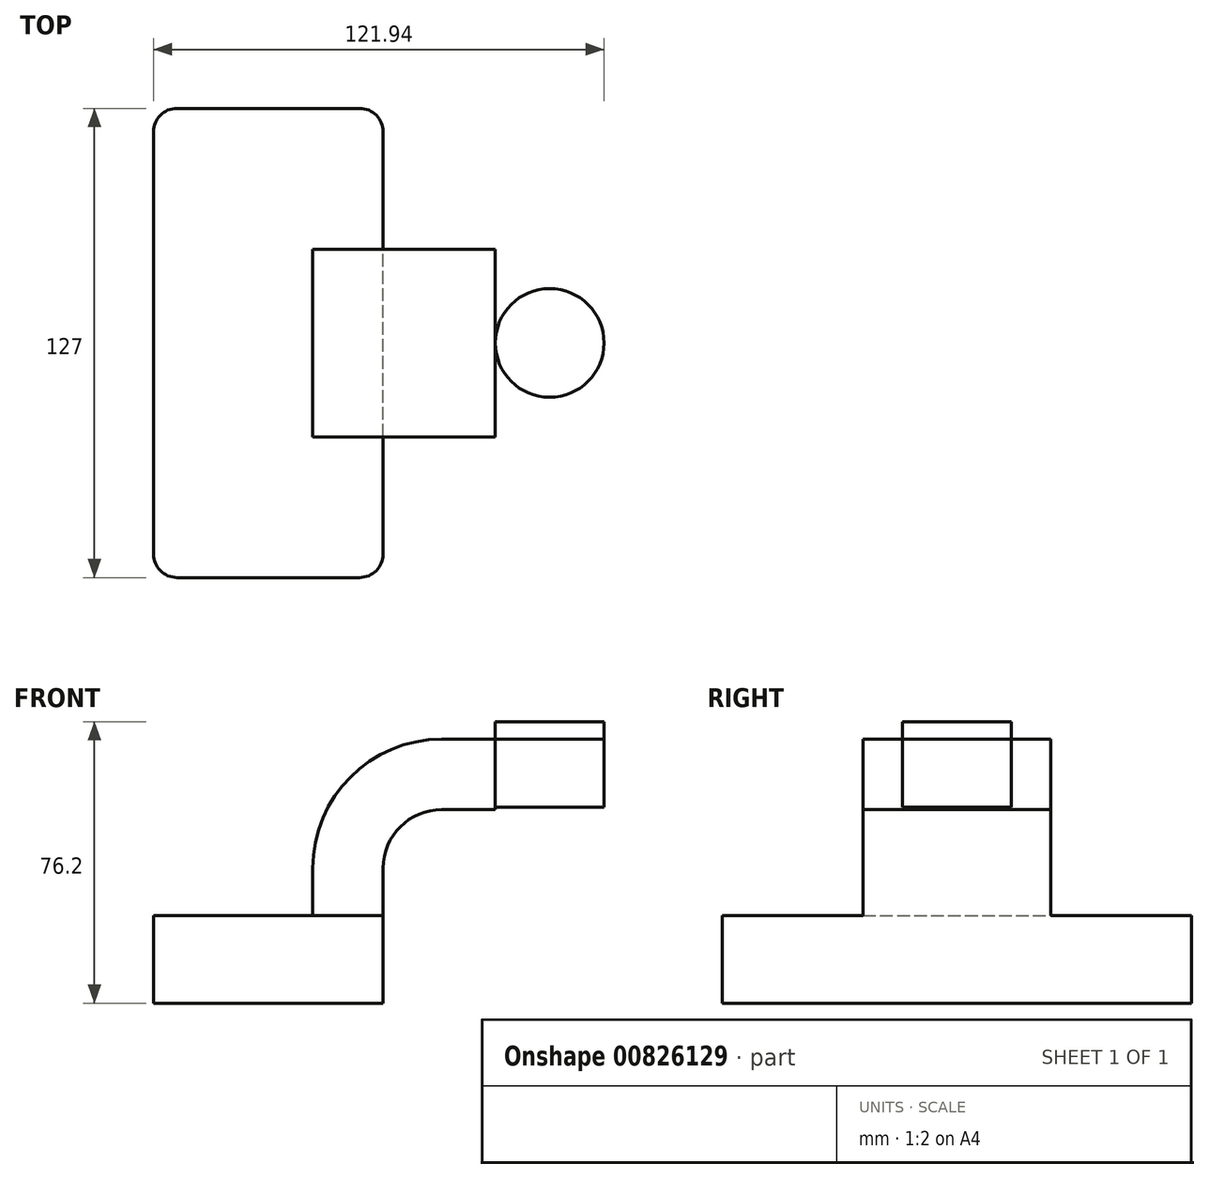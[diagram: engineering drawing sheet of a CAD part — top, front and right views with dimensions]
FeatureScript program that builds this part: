
annotation { "Feature Type Name" : "Feature", "Feature Type Description" : "" }
export const myFeature = defineFeature(function(context is Context, id is Id, definition is map)
    precondition{}
    {
        {
            var Q0;
            Q0=qCreatedBy(makeId("Front.planeOp"),FACE);
            var sketch = newSketch(context, id + "F0", { "sketchPlane" : qUnion([Q0])});
            skLineSegment(sketch, "E0.bottom", {"start": v(-31.07, 11.83) * mm, "end": v(31.07, 11.83) * mm});
            skLineSegment(sketch, "E0.top", {"start": v(-31.07, -11.83) * mm, "end": v(31.07, -11.83) * mm});
            skLineSegment(sketch, "E0.left", {"start": v(-31.07, 11.83) * mm, "end": v(-31.07, -11.83) * mm});
            skLineSegment(sketch, "E0.right", {"start": v(31.07, 11.83) * mm, "end": v(31.07, -11.83) * mm});
            skPoint(sketch, "E0.middle", {"position": v(0, 0) * mm});
            skLineSegment(sketch, "E1.bottom", {"start": v(61.43, 64.37) * mm, "end": v(112.23, 64.37) * mm});
            skLineSegment(sketch, "E1.top", {"start": v(61.43, 34.51) * mm, "end": v(112.23, 34.51) * mm});
            skLineSegment(sketch, "E1.left", {"start": v(61.43, 64.37) * mm, "end": v(61.43, 34.51) * mm});
            skLineSegment(sketch, "E1.right", {"start": v(112.23, 64.37) * mm, "end": v(112.23, 34.51) * mm});
            skPoint(sketch, "E1.middle", {"position": v(86.83, 49.44) * mm});
            skLineSegment(sketch, "E2", {"start": v(31.07, 11.83) * mm, "end": v(31.07, 24.7) * mm});
            skArc(sketch, "E3", {"start": v(31.07, 24.7) * mm, "mid": v(35.72, 35.92) * mm, "end": v(46.95, 40.57) * mm});
            skLineSegment(sketch, "E4", {"start": v(46.95, 40.57) * mm, "end": v(76.15, 40.57) * mm});
            skLineSegment(sketch, "E5.0", {"start": v(46.95, 59.62) * mm, "end": v(76.15, 59.62) * mm});
            skArc(sketch, "E5.1", {"start": v(12.02, 24.7) * mm, "mid": v(22.25, 49.39) * mm, "end": v(46.95, 59.62) * mm});
            skLineSegment(sketch, "E5.2", {"start": v(12.02, 11.83) * mm, "end": v(12.02, 24.7) * mm});
            skLineSegment(sketch, "E6", {"start": v(76.15, 40.57) * mm, "end": v(76.15, 64.37) * mm});
            skFitSpline(sketch, "E7", {"points": [v(-31.07, 11.83) * mm, v(46.95, 59.62) * mm], "startDerivative": vector(0.85, 118.43) * mm, "endDerivative": vector(92.63, -3.41) * mm});
            skSolve(sketch);
        }
        {
            var Q0;
            Q0=makeQuery(id+"F0.imprint","IMPRINT",FACE,{"disambiguationData":[TD([[makeQuery(id+"F0.imprint","IMPRINT",EDGE,{"derivedFrom":sQuery(id+"F0.wireOp",EDGE,"E0.top")}),1.0]])]});
            extrude(context, id + "F1", {"entities" : qUnion([Q0]), "depth" : 127 * mm, "offsetDistance" : 25.4 * mm, "symmetric" : true});
        }
        {
            var Q0;
            {var subQ1=sQuery(id+"F0.wireOp",EDGE,"E2");Q0=makeQuery(id+"F0.imprint","IMPRINT",FACE,{"disambiguationData":[TD([[makeQuery(id+"F0.imprint","IMPRINT",EDGE,{"derivedFrom":subQ1}),1.0]])]});}
            extrude(context, id + "F2", {"entities" : qUnion([Q0]), "operationType" : NewBodyOperationType.ADD, "depth" : 50.8 * mm, "offsetDistance" : 25.4 * mm, "symmetric" : true});
        }
        {
            var Q0;
            Q0=makeQuery(id+"F0.imprint","IMPRINT",FACE,{"disambiguationData":[TD([[makeQuery(id+"F0.imprint","IMPRINT",EDGE,{"derivedFrom":sQuery(id+"F0.wireOp",EDGE,"E5.1")}),1.0]])]});
            extrude(context, id + "F3", {"entities" : qUnion([Q0]), "operationType" : NewBodyOperationType.ADD, "depth" : 15.88 * mm, "offsetDistance" : 25.4 * mm, "symmetric" : true});
        }
        {
            var Q0;
            {var subQ0=sQuery(id+"F0.wireOp",EDGE,"E1.left");var subQ1=sQuery(id+"F0.wireOp",EDGE,"E1.bottom");var subQ2=makeQuery(id+"F0.imprint","INTERSECT",VERTEX,{"derivedFrom":[subQ1,subQ0]});Q0=makeQuery(id+"F0.imprint","IMPRINT",FACE,{"disambiguationData":[TD([[makeQuery(id+"F0.imprint","IMPRINT",EDGE,{"disambiguationData":[TD([[subQ2,-1.0]])],"derivedFrom":subQ1}),-1.0]])]});}
            var Q1;
            Q1=sQuery(id+"F0.wireOp",EDGE,"E6");
            revolve(context, id + "F4", {"surfaceOperationType" : NewSurfaceOperationType.NEW, "entities" : qUnion([Q0]), "axis" : qUnion([Q1]), "revolveType" : RevolveType.FULL});
        }
        {
            var Q0;
            Q0=makeQuery(id+"F4.opRevolve","SWEPT_FACE",FACE,{"disambiguationData":[OSD([sQuery(id+"F0.wireOp",EDGE,"E1.bottom")])]});
            extrude(context, id + "F5", {"entities" : qUnion([Q0]), "oppositeDirection" : true, "depth" : 23.1 * mm, "offsetDistance" : 25.4 * mm});
        }
        {
            var Q0;
            Q0=makeQuery(id+"F1.opExtrude","CAP_EDGE",EDGE,{"disambiguationData":[OSD([sQuery(id+"F0.wireOp",EDGE,"E0.right")])],"isStart":false});
            var Q1;
            Q1=makeQuery(id+"F1.opExtrude","CAP_EDGE",EDGE,{"disambiguationData":[OSD([sQuery(id+"F0.wireOp",EDGE,"E0.right")])],"isStart":true});
            var Q2;
            Q2=makeQuery(id+"F1.opExtrude","CAP_EDGE",EDGE,{"disambiguationData":[OSD([sQuery(id+"F0.wireOp",EDGE,"E0.left")])],"isStart":true});
            var Q3;
            Q3=makeQuery(id+"F1.opExtrude","CAP_EDGE",EDGE,{"disambiguationData":[OSD([sQuery(id+"F0.wireOp",EDGE,"E0.left")])],"isStart":false});
            fillet(context, id + "F6", {"entities" : qUnion([Q0, Q1, Q2, Q3]), "radius" : 6.35 * mm, "tangentPropagation" : true, "allowEdgeOverflow" : false});
        }
    });
